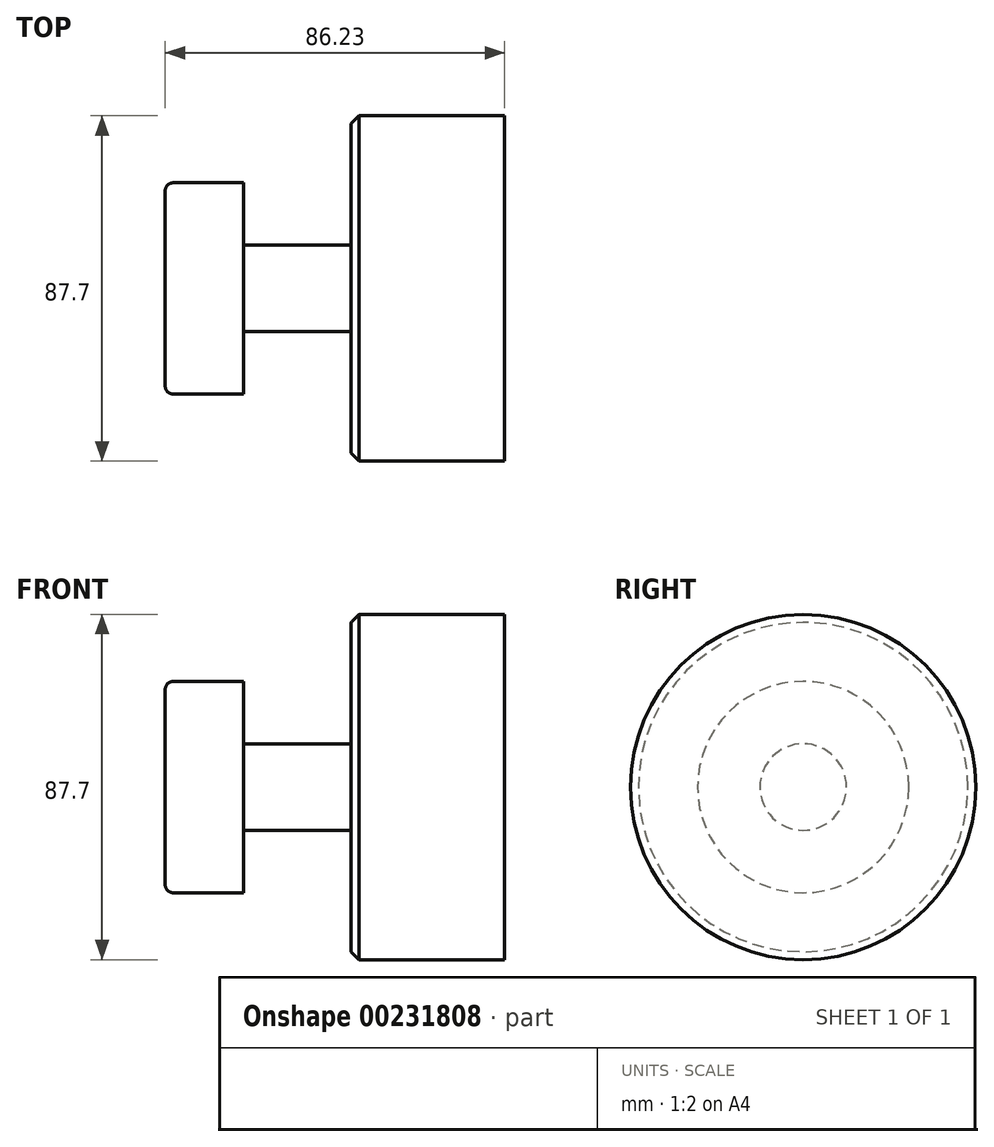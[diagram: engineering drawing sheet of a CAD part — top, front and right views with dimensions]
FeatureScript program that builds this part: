
annotation { "Feature Type Name" : "Feature", "Feature Type Description" : "" }
export const myFeature = defineFeature(function(context is Context, id is Id, definition is map)
    precondition{}
    {
        {
            var Q0;
            Q0=qCreatedBy(makeId("Front.planeOp"),FACE);
            var sketch = newSketch(context, id + "F0", { "sketchPlane" : qUnion([Q0])});
            skLineSegment(sketch, "E0", {"start": v(0, 0) * mm, "end": v(86.23, 0) * mm});
            skLineSegment(sketch, "E1", {"start": v(0, 0) * mm, "end": v(0, 26.84) * mm});
            skLineSegment(sketch, "E2", {"start": v(19.94, 26.84) * mm, "end": v(0, 26.84) * mm});
            skLineSegment(sketch, "E3", {"start": v(19.94, 26.84) * mm, "end": v(19.94, 11) * mm});
            skLineSegment(sketch, "E4", {"start": v(19.94, 11) * mm, "end": v(47.22, 11) * mm});
            skLineSegment(sketch, "E5", {"start": v(47.22, 11) * mm, "end": v(47.22, 43.85) * mm});
            skLineSegment(sketch, "E6", {"start": v(47.22, 43.85) * mm, "end": v(86.23, 43.85) * mm});
            skLineSegment(sketch, "E7", {"start": v(86.23, 43.85) * mm, "end": v(86.23, 0) * mm});
            skSolve(sketch);
        }
        {
            var Q0;
            Q0=makeQuery(id+"F0.imprint","IMPRINT",FACE,{"disambiguationData":[TD([[makeQuery(id+"F0.imprint","IMPRINT",EDGE,{"derivedFrom":sQuery(id+"F0.wireOp",EDGE,"E0")}),1.0]])]});
            var Q1;
            Q1=sQuery(id+"F0.wireOp",EDGE,"E0");
            revolve(context, id + "F1", {"entities" : qUnion([Q0]), "axis" : qUnion([Q1]), "revolveType" : RevolveType.FULL});
        }
        {
            var Q0;
            Q0=makeQuery(id+"F1.opRevolve","SWEPT_EDGE",EDGE,{"disambiguationData":[OSD([sQuery(id+"F0.wireOp",EDGE,"E1"),sQuery(id+"F0.wireOp",EDGE,"E2")])]});
            fillet(context, id + "F2", {"entities" : qUnion([Q0]), "radius" : 2 * mm, "tangentPropagation" : true, "allowEdgeOverflow" : false});
        }
        {
            var Q0;
            Q0=makeQuery(id+"F1.opRevolve","SWEPT_EDGE",EDGE,{"disambiguationData":[OSD([sQuery(id+"F0.wireOp",EDGE,"E5"),sQuery(id+"F0.wireOp",EDGE,"E6")])]});
            chamfer(context, id + "F3", {"entities" : qUnion([Q0]), "width" : 2 * mm, "tangentPropagation" : true});
        }
    });
